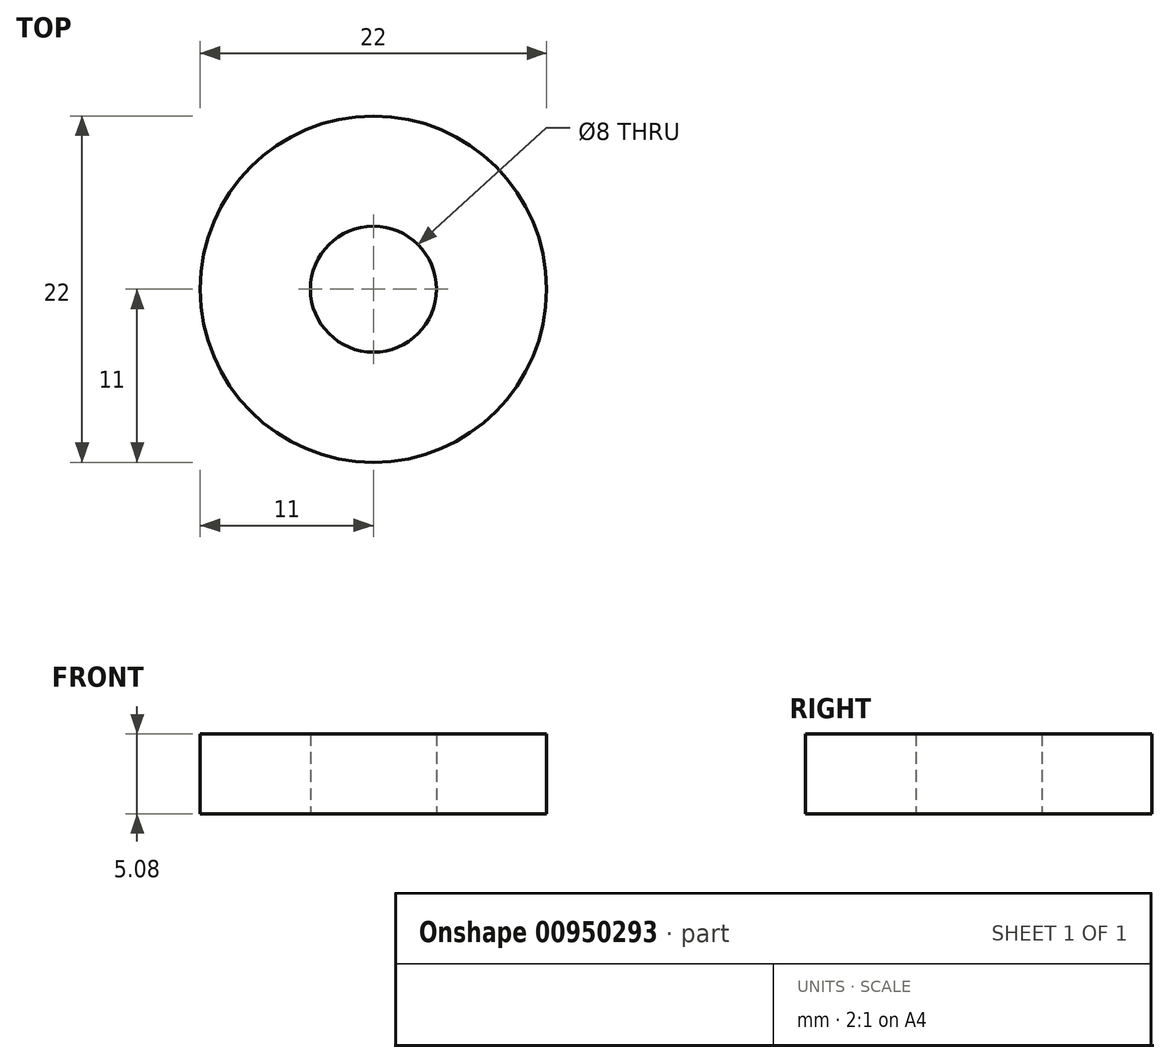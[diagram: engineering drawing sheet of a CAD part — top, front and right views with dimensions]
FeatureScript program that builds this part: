
annotation { "Feature Type Name" : "Feature", "Feature Type Description" : "" }
export const myFeature = defineFeature(function(context is Context, id is Id, definition is map)
    precondition{}
    {
        {
            var Q0;
            Q0=qCreatedBy(makeId("Front.planeOp"),FACE);
            var sketch = newSketch(context, id + "F0", { "sketchPlane" : qUnion([Q0])});
            skLineSegment(sketch, "E0.bottom", {"start": v(3.5, 2.54) * mm, "end": v(-3.5, 2.54) * mm});
            skLineSegment(sketch, "E0.top", {"start": v(3.5, -2.54) * mm, "end": v(-3.5, -2.54) * mm});
            skLineSegment(sketch, "E0.left", {"start": v(3.5, 2.54) * mm, "end": v(3.5, -2.54) * mm});
            skLineSegment(sketch, "E0.right", {"start": v(-3.5, 2.54) * mm, "end": v(-3.5, -2.54) * mm});
            skPoint(sketch, "E0.middle", {"position": v(0, 0) * mm});
            skSolve(sketch);
        }
        {
            var Q0;
            Q0=qCreatedBy(makeId("Front.planeOp"),FACE);
            var sketch = newSketch(context, id + "F1", { "sketchPlane" : qUnion([Q0])});
            skLineSegment(sketch, "E1", {"start": v(-7.5, 0) * mm, "end": v(-7.5, 5.76) * mm});
            skLineSegment(sketch, "E2", {"start": v(0, 0) * mm, "end": v(0, 5.88) * mm});
            skSolve(sketch);
        }
        {
            var Q0;
            Q0=makeQuery(id+"F0.imprint","IMPRINT",FACE,{"disambiguationData":[TD([[makeQuery(id+"F0.imprint","IMPRINT",EDGE,{"derivedFrom":sQuery(id+"F0.wireOp",EDGE,"E0.bottom")}),1.0]])]});
            var Q1;
            Q1=sQuery(id+"F1.wireOp",EDGE,"E1");
            revolve(context, id + "F2", {"surfaceOperationType" : NewSurfaceOperationType.NEW, "entities" : qUnion([Q0]), "axis" : qUnion([Q1]), "revolveType" : RevolveType.FULL});
        }
    });
